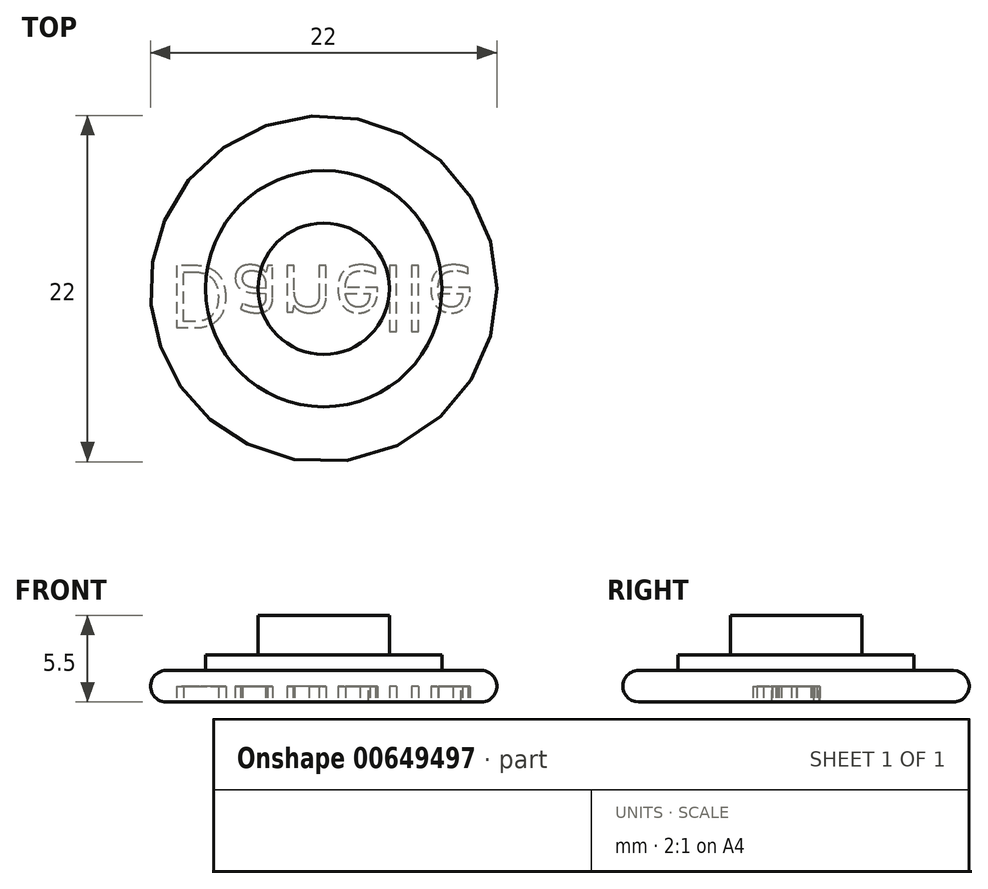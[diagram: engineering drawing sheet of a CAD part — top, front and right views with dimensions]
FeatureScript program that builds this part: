
annotation { "Feature Type Name" : "Feature", "Feature Type Description" : "" }
export const myFeature = defineFeature(function(context is Context, id is Id, definition is map)
    precondition{}
    {
        {
            var Q0;
            Q0=qCreatedBy(makeId("Top.planeOp"),FACE);
            var sketch = newSketch(context, id + "F0", { "sketchPlane" : qUnion([Q0])});
            skCircle(sketch, "E0", {"center": v(0, 0) * mm, "radius": 11 * mm});
            skCircle(sketch, "E1", {"center": v(0, 0) * mm, "radius": 7.5 * mm});
            skCircle(sketch, "E2", {"center": v(0, 0) * mm, "radius": 4.17 * mm});
            skSolve(sketch);
        }
        {
            var Q0;
            Q0=makeQuery(id+"F0.imprint","IMPRINT",FACE,{"disambiguationData":[TD([[makeQuery(id+"F0.imprint","IMPRINT",EDGE,{"derivedFrom":sQuery(id+"F0.wireOp",EDGE,"E0")}),1.0]])]});
            extrude(context, id + "F1", {"entities" : qUnion([Q0]), "depth" : 2 * mm, "offsetDistance" : 25 * mm});
        }
        {
            var Q0;
            Q0=makeQuery(id+"F0.imprint","IMPRINT",FACE,{"disambiguationData":[TD([[makeQuery(id+"F0.imprint","IMPRINT",EDGE,{"derivedFrom":sQuery(id+"F0.wireOp",EDGE,"E1")}),1.0]])]});
            extrude(context, id + "F2", {"entities" : qUnion([Q0]), "operationType" : NewBodyOperationType.ADD, "depth" : 3 * mm, "offsetDistance" : 25 * mm});
        }
        {
            var Q0;
            Q0=makeQuery(id+"F0.imprint","IMPRINT",FACE,{"disambiguationData":[TD([[makeQuery(id+"F0.imprint","IMPRINT",EDGE,{"derivedFrom":sQuery(id+"F0.wireOp",EDGE,"E2")}),1.0]])]});
            extrude(context, id + "F3", {"entities" : qUnion([Q0]), "operationType" : NewBodyOperationType.ADD, "depth" : 5.5 * mm, "offsetDistance" : 25 * mm});
        }
        {
            var Q0;
            Q0=makeQuery(id+"F1.opExtrude","CAP_EDGE",EDGE,{"disambiguationData":[OSD([sQuery(id+"F0.wireOp",EDGE,"E0")])],"isStart":false});
            var Q1;
            Q1=makeQuery(id+"F1.opExtrude","CAP_EDGE",EDGE,{"disambiguationData":[OSD([sQuery(id+"F0.wireOp",EDGE,"E0")])],"isStart":true});
            fillet(context, id + "F4", {"entities" : qUnion([Q0, Q1]), "radius" : 1 * mm, "tangentPropagation" : true, "allowEdgeOverflow" : false});
        }
        {
            var Q0;
            {var subQ0=sQuery(id+"F0.wireOp",EDGE,"E2");var subQ1=sQuery(id+"F0.wireOp",EDGE,"E1");Q0=makeQuery(id+"F3.boolean.opBoolean","MERGE",FACE,{"derivedFrom":[makeQuery(id+"F2.boolean.opBoolean","MERGE",FACE,{"derivedFrom":[makeQuery(id+"F1.opExtrude","CAP_FACE",FACE,{"disambiguationData":[OSD([sQuery(id+"F0.wireOp",EDGE,"E0"),subQ1])],"isStart":true}),makeQuery(id+"F2.opExtrude","CAP_FACE",FACE,{"disambiguationData":[OSD([subQ1,subQ0])],"isStart":true})]}),makeQuery(id+"F3.opExtrude","CAP_FACE",FACE,{"disambiguationData":[OSD([subQ0])],"isStart":true})]});}
            var sketch = newSketch(context, id + "F5", { "sketchPlane" : qUnion([Q0])});
            skText(sketch, "E3", { "text": "Danelle", "fontName": "OpenSans-Regular.ttf"});
            const initialGuessF5  = {"E3": [-0.0099, -0.00147, 1, 0, 0.00398]};
            skSetInitialGuess(sketch, initialGuessF5);
            skSolve(sketch);
        }
        {
            var Q0;
            Q0 = qSketchRegion(id + "F5", true);
            extrude(context, id + "F6", {"entities" : qUnion([Q0]), "operationType" : NewBodyOperationType.REMOVE, "oppositeDirection" : true, "depth" : 1 * mm, "offsetDistance" : 25 * mm});
        }
    });
